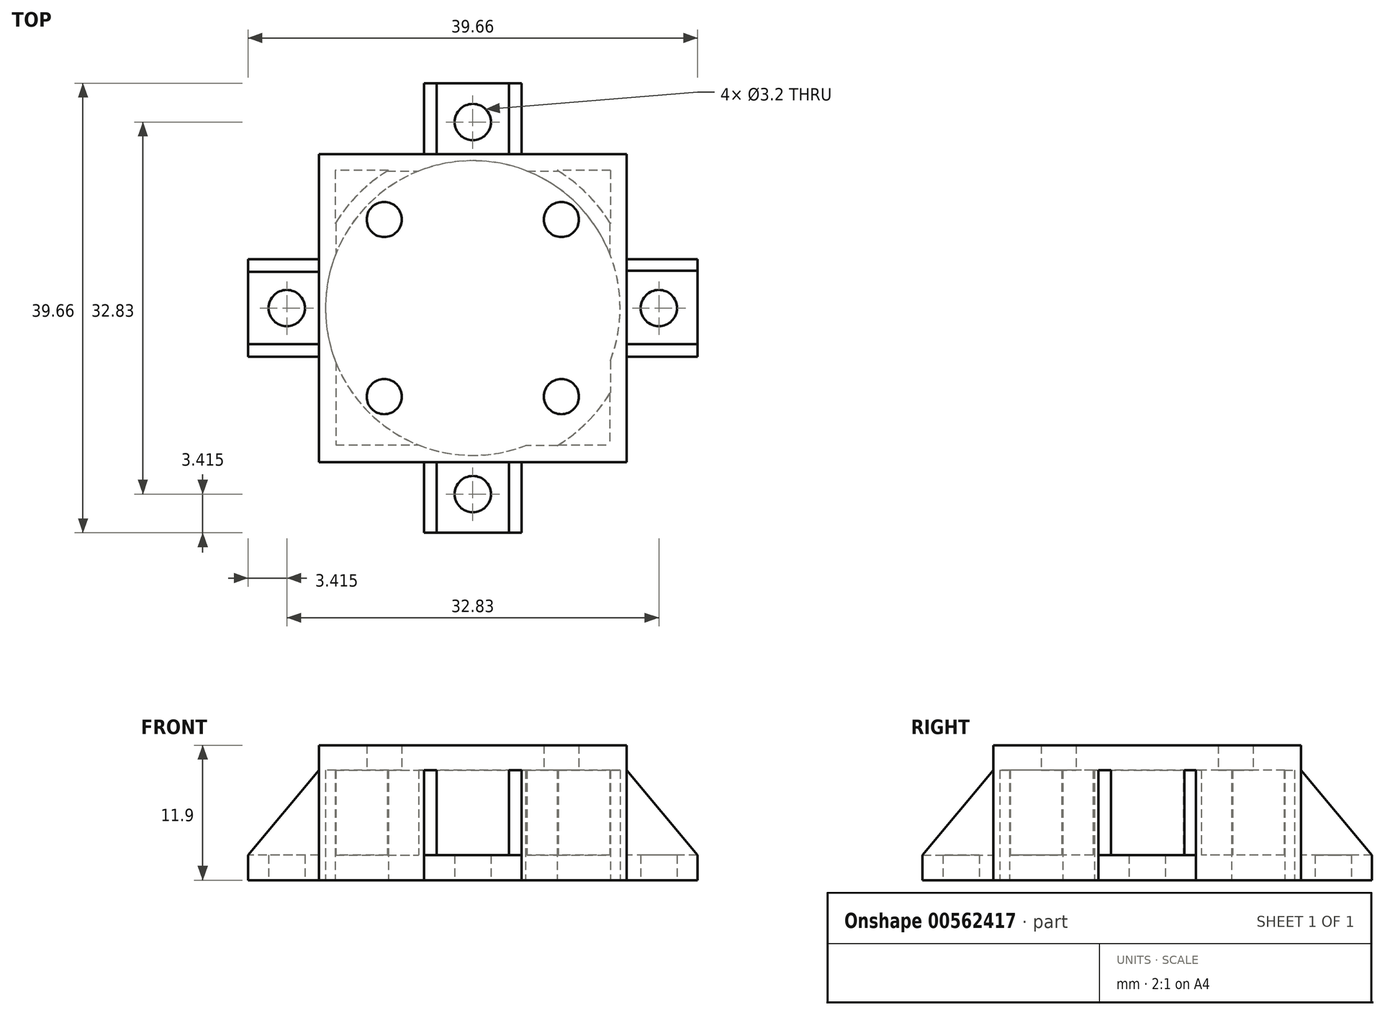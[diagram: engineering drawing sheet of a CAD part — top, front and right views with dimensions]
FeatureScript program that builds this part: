
annotation { "Feature Type Name" : "Feature", "Feature Type Description" : "" }
export const myFeature = defineFeature(function(context is Context, id is Id, definition is map)
    precondition{}
    {
        {
            var Q0;
            Q0=qCreatedBy(makeId("Top.planeOp"),FACE);
            var sketch = newSketch(context, id + "F0", { "sketchPlane" : qUnion([Q0])});
            skCircle(sketch, "E0", {"center": v(0, 0) * mm, "radius": 13 * mm});
            skLineSegment(sketch, "E1", {"start": v(0, 19.83) * mm, "end": v(4.3, 19.83) * mm});
            skLineSegment(sketch, "E2", {"start": v(4.3, 19.83) * mm, "end": v(4.3, 12.27) * mm});
            skLineSegment(sketch, "E3.MirrorCS", {"start": v(0, 19.83) * mm, "end": v(-4.3, 19.83) * mm});
            skLineSegment(sketch, "E4.MirrorCS", {"start": v(-4.3, 19.83) * mm, "end": v(-4.3, 12.27) * mm});
            skLineSegment(sketch, "E5", {"start": v(0, 0) * mm, "end": v(27.32, 0) * mm, "construction": true});
            skLineSegment(sketch, "E6", {"start": v(0, 0) * mm, "end": v(27.32, 27.32) * mm, "construction": true});
            skLineSegment(sketch, "E7", {"start": v(0, 19.83) * mm, "end": v(0, 13) * mm, "construction": true});
            skCircle(sketch, "E8", {"center": v(0, 16.42) * mm, "radius": 1.6 * mm});
            skLineSegment(sketch, "E9.MirrorCS", {"start": v(19.83, 0) * mm, "end": v(19.83, 4.3) * mm});
            skLineSegment(sketch, "E10.MirrorCS", {"start": v(19.83, 0) * mm, "end": v(19.83, -4.3) * mm});
            skLineSegment(sketch, "E11.MirrorCS", {"start": v(19.83, -4.3) * mm, "end": v(12.27, -4.3) * mm});
            skCircle(sketch, "E12.MirrorC", {"center": v(16.42, 0) * mm, "radius": 1.6 * mm});
            skLineSegment(sketch, "E13.MirrorCS", {"start": v(19.83, 4.3) * mm, "end": v(12.27, 4.3) * mm});
            skLineSegment(sketch, "E14.MirrorCS", {"start": v(0, -19.83) * mm, "end": v(4.3, -19.83) * mm});
            skLineSegment(sketch, "E15.MirrorCS", {"start": v(0, -19.83) * mm, "end": v(-4.3, -19.83) * mm});
            skLineSegment(sketch, "E16.MirrorCS", {"start": v(-4.3, -19.83) * mm, "end": v(-4.3, -12.27) * mm});
            skLineSegment(sketch, "E17.MirrorCS", {"start": v(4.3, -19.83) * mm, "end": v(4.3, -12.27) * mm});
            skCircle(sketch, "E18.MirrorC", {"center": v(0, -16.42) * mm, "radius": 1.6 * mm});
            skLineSegment(sketch, "E19", {"start": v(0, 0) * mm, "end": v(0, -28.1) * mm, "construction": true});
            skLineSegment(sketch, "E20.MirrorCS", {"start": v(-19.83, 4.3) * mm, "end": v(-12.27, 4.3) * mm});
            skLineSegment(sketch, "E21.MirrorCS", {"start": v(-19.83, 0) * mm, "end": v(-19.83, 4.3) * mm});
            skCircle(sketch, "E22.MirrorC", {"center": v(-16.42, 0) * mm, "radius": 1.6 * mm});
            skLineSegment(sketch, "E23.MirrorCS", {"start": v(-19.83, 0) * mm, "end": v(-19.83, -4.3) * mm});
            skLineSegment(sketch, "E24.MirrorCS", {"start": v(-19.83, -4.3) * mm, "end": v(-12.27, -4.3) * mm});
            skCircle(sketch, "E25", {"center": v(0, 0) * mm, "radius": 14.25 * mm});
            skLineSegment(sketch, "E26", {"start": v(-4.3, 13.59) * mm, "end": v(-13.59, 13.59) * mm});
            skLineSegment(sketch, "E27", {"start": v(-13.59, 13.59) * mm, "end": v(-13.59, 4.3) * mm});
            skLineSegment(sketch, "E28.MirrorCS", {"start": v(13.59, -4.3) * mm, "end": v(13.59, -13.59) * mm});
            skLineSegment(sketch, "E29.MirrorCS", {"start": v(13.59, -13.59) * mm, "end": v(4.3, -13.59) * mm});
            skLineSegment(sketch, "E30.MirrorCS", {"start": v(13.59, 4.3) * mm, "end": v(13.59, 13.59) * mm});
            skLineSegment(sketch, "E31.MirrorCS", {"start": v(13.59, 13.59) * mm, "end": v(4.3, 13.59) * mm});
            skLineSegment(sketch, "E32.MirrorCS", {"start": v(-4.3, -13.59) * mm, "end": v(-13.59, -13.59) * mm});
            skLineSegment(sketch, "E33.MirrorCS", {"start": v(-13.59, -13.59) * mm, "end": v(-13.59, -4.3) * mm});
            skLineSegment(sketch, "E34.bottom", {"start": v(12.14, 12.14) * mm, "end": v(-12.14, 12.14) * mm});
            skLineSegment(sketch, "E34.top", {"start": v(12.14, -12.14) * mm, "end": v(-12.14, -12.14) * mm});
            skLineSegment(sketch, "E34.left", {"start": v(12.14, 12.14) * mm, "end": v(12.14, -12.14) * mm});
            skLineSegment(sketch, "E34.right", {"start": v(-12.14, 12.14) * mm, "end": v(-12.14, -12.14) * mm});
            skSolve(sketch);
        }
        {
            var Q0;
            {var subQ5=sQuery(id+"F0.wireOp",EDGE,"E1");Q0=makeQuery(id+"F0.imprint","IMPRINT",FACE,{"disambiguationData":[TD([[makeQuery(id+"F0.imprint","IMPRINT",EDGE,{"derivedFrom":subQ5}),-1.0]])]});}
            var Q1;
            {var subQ0=sQuery(id+"F0.wireOp",EDGE,"E4.MirrorCS");var subQ1=sQuery(id+"F0.wireOp",EDGE,"E0");var subQ2=makeQuery(id+"F0.imprint","INTERSECT",VERTEX,{"derivedFrom":[subQ1,subQ0]});Q1=makeQuery(id+"F0.imprint","IMPRINT",FACE,{"disambiguationData":[TD([[makeQuery(id+"F0.imprint","IMPRINT",EDGE,{"disambiguationData":[TD([[subQ2,-1.0]])],"derivedFrom":subQ1}),-1.0]])]});}
            var Q2;
            {var subQ0=sQuery(id+"F0.wireOp",EDGE,"E2");var subQ1=sQuery(id+"F0.wireOp",EDGE,"E0");var subQ2=makeQuery(id+"F0.imprint","INTERSECT",VERTEX,{"derivedFrom":[subQ1,subQ0]});Q2=makeQuery(id+"F0.imprint","IMPRINT",FACE,{"disambiguationData":[TD([[makeQuery(id+"F0.imprint","IMPRINT",EDGE,{"disambiguationData":[TD([[subQ2,-1.0]])],"derivedFrom":subQ1}),-1.0]])]});}
            var Q3;
            {var subQ0=sQuery(id+"F0.wireOp",EDGE,"E2");var subQ1=sQuery(id+"F0.wireOp",EDGE,"E0");var subQ2=makeQuery(id+"F0.imprint","INTERSECT",VERTEX,{"derivedFrom":[subQ1,subQ0]});Q3=makeQuery(id+"F0.imprint","IMPRINT",FACE,{"disambiguationData":[TD([[makeQuery(id+"F0.imprint","IMPRINT",EDGE,{"disambiguationData":[TD([[subQ2,1.0]])],"derivedFrom":subQ1}),-1.0]])]});}
            var Q4;
            {var subQ0=sQuery(id+"F0.wireOp",EDGE,"E11.MirrorCS");var subQ1=sQuery(id+"F0.wireOp",EDGE,"E0");var subQ2=makeQuery(id+"F0.imprint","INTERSECT",VERTEX,{"derivedFrom":[subQ1,subQ0]});Q4=makeQuery(id+"F0.imprint","IMPRINT",FACE,{"disambiguationData":[TD([[makeQuery(id+"F0.imprint","IMPRINT",EDGE,{"disambiguationData":[TD([[subQ2,-1.0]])],"derivedFrom":subQ1}),-1.0]])]});}
            var Q5;
            {var subQ4=sQuery(id+"F0.wireOp",EDGE,"E9.MirrorCS");Q5=makeQuery(id+"F0.imprint","IMPRINT",FACE,{"disambiguationData":[TD([[makeQuery(id+"F0.imprint","IMPRINT",EDGE,{"derivedFrom":subQ4}),1.0]])]});}
            var Q6;
            {var subQ0=sQuery(id+"F0.wireOp",EDGE,"E11.MirrorCS");var subQ1=sQuery(id+"F0.wireOp",EDGE,"E0");var subQ2=makeQuery(id+"F0.imprint","INTERSECT",VERTEX,{"derivedFrom":[subQ1,subQ0]});Q6=makeQuery(id+"F0.imprint","IMPRINT",FACE,{"disambiguationData":[TD([[makeQuery(id+"F0.imprint","IMPRINT",EDGE,{"disambiguationData":[TD([[subQ2,1.0]])],"derivedFrom":subQ1}),-1.0]])]});}
            var Q7;
            {var subQ0=sQuery(id+"F0.wireOp",EDGE,"E16.MirrorCS");var subQ1=sQuery(id+"F0.wireOp",EDGE,"E0");var subQ2=makeQuery(id+"F0.imprint","INTERSECT",VERTEX,{"derivedFrom":[subQ1,subQ0]});Q7=makeQuery(id+"F0.imprint","IMPRINT",FACE,{"disambiguationData":[TD([[makeQuery(id+"F0.imprint","IMPRINT",EDGE,{"disambiguationData":[TD([[subQ2,-1.0]])],"derivedFrom":subQ1}),-1.0]])]});}
            var Q8;
            {var subQ0=sQuery(id+"F0.wireOp",EDGE,"E16.MirrorCS");var subQ1=sQuery(id+"F0.wireOp",EDGE,"E0");var subQ2=makeQuery(id+"F0.imprint","INTERSECT",VERTEX,{"derivedFrom":[subQ1,subQ0]});Q8=makeQuery(id+"F0.imprint","IMPRINT",FACE,{"disambiguationData":[TD([[makeQuery(id+"F0.imprint","IMPRINT",EDGE,{"disambiguationData":[TD([[subQ2,1.0]])],"derivedFrom":subQ1}),-1.0]])]});}
            var Q9;
            {var subQ0=sQuery(id+"F0.wireOp",EDGE,"E20.MirrorCS");var subQ1=sQuery(id+"F0.wireOp",EDGE,"E0");var subQ2=makeQuery(id+"F0.imprint","INTERSECT",VERTEX,{"derivedFrom":[subQ1,subQ0]});Q9=makeQuery(id+"F0.imprint","IMPRINT",FACE,{"disambiguationData":[TD([[makeQuery(id+"F0.imprint","IMPRINT",EDGE,{"disambiguationData":[TD([[subQ2,-1.0]])],"derivedFrom":subQ1}),-1.0]])]});}
            var Q10;
            {var subQ1=sQuery(id+"F0.wireOp",EDGE,"E21.MirrorCS");Q10=makeQuery(id+"F0.imprint","IMPRINT",FACE,{"disambiguationData":[TD([[makeQuery(id+"F0.imprint","IMPRINT",EDGE,{"derivedFrom":subQ1}),-1.0]])]});}
            var Q11;
            {var subQ1=sQuery(id+"F0.wireOp",EDGE,"E14.MirrorCS");Q11=makeQuery(id+"F0.imprint","IMPRINT",FACE,{"disambiguationData":[TD([[makeQuery(id+"F0.imprint","IMPRINT",EDGE,{"derivedFrom":subQ1}),1.0]])]});}
            var Q12;
            {var subQ0=sQuery(id+"F0.wireOp",EDGE,"E34.bottom");var subQ1=sQuery(id+"F0.wireOp",EDGE,"E25");var subQ2=makeQuery(id+"F0.imprint","INTERSECT",VERTEX,{"disambiguationData":[OD(1.0)],"derivedFrom":[subQ1,subQ0]});Q12=makeQuery(id+"F0.imprint","IMPRINT",FACE,{"disambiguationData":[TD([[makeQuery(id+"F0.imprint","IMPRINT",EDGE,{"disambiguationData":[TD([[subQ2,-1.0]])],"derivedFrom":subQ1}),-1.0]])]});}
            var Q13;
            {var subQ0=sQuery(id+"F0.wireOp",EDGE,"E32.MirrorCS");Q13=makeQuery(id+"F0.imprint","IMPRINT",FACE,{"disambiguationData":[TD([[makeQuery(id+"F0.imprint","IMPRINT",EDGE,{"derivedFrom":subQ0}),-1.0]])]});}
            var Q14;
            {var subQ0=sQuery(id+"F0.wireOp",EDGE,"E34.right");var subQ1=sQuery(id+"F0.wireOp",EDGE,"E25");var subQ2=makeQuery(id+"F0.imprint","INTERSECT",VERTEX,{"disambiguationData":[OD(1.0)],"derivedFrom":[subQ1,subQ0]});Q14=makeQuery(id+"F0.imprint","IMPRINT",FACE,{"disambiguationData":[TD([[makeQuery(id+"F0.imprint","IMPRINT",EDGE,{"disambiguationData":[TD([[subQ2,-1.0]])],"derivedFrom":subQ1}),-1.0]])]});}
            var Q15;
            {var subQ0=sQuery(id+"F0.wireOp",EDGE,"E24.MirrorCS");var subQ1=sQuery(id+"F0.wireOp",EDGE,"E0");var subQ2=makeQuery(id+"F0.imprint","INTERSECT",VERTEX,{"derivedFrom":[subQ1,subQ0]});Q15=makeQuery(id+"F0.imprint","IMPRINT",FACE,{"disambiguationData":[TD([[makeQuery(id+"F0.imprint","IMPRINT",EDGE,{"disambiguationData":[TD([[subQ2,-1.0]])],"derivedFrom":subQ1}),-1.0]])]});}
            var Q16;
            {var subQ7=sQuery(id+"F0.wireOp",EDGE,"E26");Q16=makeQuery(id+"F0.imprint","IMPRINT",FACE,{"disambiguationData":[TD([[makeQuery(id+"F0.imprint","IMPRINT",EDGE,{"derivedFrom":subQ7}),1.0]])]});}
            var Q17;
            {var subQ6=sQuery(id+"F0.wireOp",EDGE,"E30.MirrorCS");Q17=makeQuery(id+"F0.imprint","IMPRINT",FACE,{"disambiguationData":[TD([[makeQuery(id+"F0.imprint","IMPRINT",EDGE,{"derivedFrom":subQ6}),1.0]])]});}
            var Q18;
            {var subQ0=sQuery(id+"F0.wireOp",EDGE,"E34.left");var subQ1=sQuery(id+"F0.wireOp",EDGE,"E25");var subQ2=makeQuery(id+"F0.imprint","INTERSECT",VERTEX,{"disambiguationData":[OD(0.0)],"derivedFrom":[subQ1,subQ0]});Q18=makeQuery(id+"F0.imprint","IMPRINT",FACE,{"disambiguationData":[TD([[makeQuery(id+"F0.imprint","IMPRINT",EDGE,{"disambiguationData":[TD([[subQ2,-1.0]])],"derivedFrom":subQ1}),-1.0]])]});}
            var Q19;
            {var subQ0=sQuery(id+"F0.wireOp",EDGE,"E34.left");var subQ1=sQuery(id+"F0.wireOp",EDGE,"E0");var subQ2=makeQuery(id+"F0.imprint","INTERSECT",VERTEX,{"disambiguationData":[OD(0.0)],"derivedFrom":[subQ1,subQ0]});Q19=makeQuery(id+"F0.imprint","IMPRINT",FACE,{"disambiguationData":[TD([[makeQuery(id+"F0.imprint","IMPRINT",EDGE,{"disambiguationData":[TD([[subQ2,-1.0]])],"derivedFrom":subQ1}),-1.0]])]});}
            var Q20;
            {var subQ0=sQuery(id+"F0.wireOp",EDGE,"E13.MirrorCS");var subQ1=sQuery(id+"F0.wireOp",EDGE,"E0");var subQ2=makeQuery(id+"F0.imprint","INTERSECT",VERTEX,{"derivedFrom":[subQ1,subQ0]});Q20=makeQuery(id+"F0.imprint","IMPRINT",FACE,{"disambiguationData":[TD([[makeQuery(id+"F0.imprint","IMPRINT",EDGE,{"disambiguationData":[TD([[subQ2,-1.0]])],"derivedFrom":subQ1}),-1.0]])]});}
            var Q21;
            {var subQ0=sQuery(id+"F0.wireOp",EDGE,"E34.bottom");var subQ1=sQuery(id+"F0.wireOp",EDGE,"E0");var subQ2=makeQuery(id+"F0.imprint","INTERSECT",VERTEX,{"disambiguationData":[OD(1.0)],"derivedFrom":[subQ1,subQ0]});Q21=makeQuery(id+"F0.imprint","IMPRINT",FACE,{"disambiguationData":[TD([[makeQuery(id+"F0.imprint","IMPRINT",EDGE,{"disambiguationData":[TD([[subQ2,-1.0]])],"derivedFrom":subQ1}),-1.0]])]});}
            var Q22;
            {var subQ0=sQuery(id+"F0.wireOp",EDGE,"E20.MirrorCS");var subQ1=sQuery(id+"F0.wireOp",EDGE,"E0");var subQ2=makeQuery(id+"F0.imprint","INTERSECT",VERTEX,{"derivedFrom":[subQ1,subQ0]});Q22=makeQuery(id+"F0.imprint","IMPRINT",FACE,{"disambiguationData":[TD([[makeQuery(id+"F0.imprint","IMPRINT",EDGE,{"disambiguationData":[TD([[subQ2,1.0]])],"derivedFrom":subQ1}),-1.0]])]});}
            var Q23;
            {var subQ0=sQuery(id+"F0.wireOp",EDGE,"E34.right");var subQ1=sQuery(id+"F0.wireOp",EDGE,"E0");var subQ2=makeQuery(id+"F0.imprint","INTERSECT",VERTEX,{"disambiguationData":[OD(1.0)],"derivedFrom":[subQ1,subQ0]});Q23=makeQuery(id+"F0.imprint","IMPRINT",FACE,{"disambiguationData":[TD([[makeQuery(id+"F0.imprint","IMPRINT",EDGE,{"disambiguationData":[TD([[subQ2,-1.0]])],"derivedFrom":subQ1}),-1.0]])]});}
            var Q24;
            {var subQ0=sQuery(id+"F0.wireOp",EDGE,"E34.top");var subQ1=sQuery(id+"F0.wireOp",EDGE,"E0");var subQ2=makeQuery(id+"F0.imprint","INTERSECT",VERTEX,{"disambiguationData":[OD(1.0)],"derivedFrom":[subQ1,subQ0]});Q24=makeQuery(id+"F0.imprint","IMPRINT",FACE,{"disambiguationData":[TD([[makeQuery(id+"F0.imprint","IMPRINT",EDGE,{"disambiguationData":[TD([[subQ2,-1.0]])],"derivedFrom":subQ1}),-1.0]])]});}
            var Q25;
            {var subQ0=sQuery(id+"F0.wireOp",EDGE,"E34.top");var subQ1=sQuery(id+"F0.wireOp",EDGE,"E25");var subQ2=makeQuery(id+"F0.imprint","INTERSECT",VERTEX,{"disambiguationData":[OD(1.0)],"derivedFrom":[subQ1,subQ0]});Q25=makeQuery(id+"F0.imprint","IMPRINT",FACE,{"disambiguationData":[TD([[makeQuery(id+"F0.imprint","IMPRINT",EDGE,{"disambiguationData":[TD([[subQ2,-1.0]])],"derivedFrom":subQ1}),-1.0]])]});}
            var Q26;
            {var subQ0=sQuery(id+"F0.wireOp",EDGE,"E28.MirrorCS");Q26=makeQuery(id+"F0.imprint","IMPRINT",FACE,{"disambiguationData":[TD([[makeQuery(id+"F0.imprint","IMPRINT",EDGE,{"derivedFrom":subQ0}),-1.0]])]});}
            var Q27;
            {var subQ0=sQuery(id+"F0.wireOp",EDGE,"E17.MirrorCS");var subQ1=sQuery(id+"F0.wireOp",EDGE,"E0");var subQ2=makeQuery(id+"F0.imprint","INTERSECT",VERTEX,{"derivedFrom":[subQ1,subQ0]});Q27=makeQuery(id+"F0.imprint","IMPRINT",FACE,{"disambiguationData":[TD([[makeQuery(id+"F0.imprint","IMPRINT",EDGE,{"disambiguationData":[TD([[subQ2,-1.0]])],"derivedFrom":subQ1}),-1.0]])]});}
            extrude(context, id + "F1", {"entities" : qUnion([Q0, Q1, Q2, Q3, Q4, Q5, Q6, Q7, Q8, Q9, Q10, Q11, Q12, Q13, Q14, Q15, Q16, Q17, Q18, Q19, Q20, Q21, Q22, Q23, Q24, Q25, Q26, Q27]), "depth" : 2.2 * mm, "offsetDistance" : 25 * mm});
        }
        {
            var Q0;
            Q0=makeQuery(id+"F1.opExtrude","CAP_FACE",FACE,{"disambiguationData":[OSD([sQuery(id+"F0.wireOp",EDGE,"E0"),sQuery(id+"F0.wireOp",EDGE,"E1"),sQuery(id+"F0.wireOp",EDGE,"E2"),sQuery(id+"F0.wireOp",EDGE,"E3.MirrorCS"),sQuery(id+"F0.wireOp",EDGE,"E4.MirrorCS"),sQuery(id+"F0.wireOp",EDGE,"E8"),sQuery(id+"F0.wireOp",EDGE,"E9.MirrorCS"),sQuery(id+"F0.wireOp",EDGE,"E10.MirrorCS"),sQuery(id+"F0.wireOp",EDGE,"E11.MirrorCS"),sQuery(id+"F0.wireOp",EDGE,"E12.MirrorC"),sQuery(id+"F0.wireOp",EDGE,"E13.MirrorCS"),sQuery(id+"F0.wireOp",EDGE,"E14.MirrorCS"),sQuery(id+"F0.wireOp",EDGE,"E15.MirrorCS"),sQuery(id+"F0.wireOp",EDGE,"E16.MirrorCS"),sQuery(id+"F0.wireOp",EDGE,"E17.MirrorCS"),sQuery(id+"F0.wireOp",EDGE,"E18.MirrorC"),sQuery(id+"F0.wireOp",EDGE,"E20.MirrorCS"),sQuery(id+"F0.wireOp",EDGE,"E21.MirrorCS"),sQuery(id+"F0.wireOp",EDGE,"E22.MirrorC"),sQuery(id+"F0.wireOp",EDGE,"E23.MirrorCS"),sQuery(id+"F0.wireOp",EDGE,"E24.MirrorCS"),sQuery(id+"F0.wireOp",EDGE,"E25")])],"isStart":false});
            var sketch = newSketch(context, id + "F2", { "sketchPlane" : qUnion([Q0])});
            skPoint(sketch, "E35.first.point", {"position": v(-13.59, 4.3) * mm});
            skPoint(sketch, "E35.second.point", {"position": v(4.3, 13.59) * mm});
            skPoint(sketch, "E35.third.point", {"position": v(4.3, -13.59) * mm});
            skLineSegment(sketch, "E36", {"start": v(-4.3, 13.59) * mm, "end": v(-4.3, 19.83) * mm});
            skLineSegment(sketch, "E37", {"start": v(-4.3, 19.83) * mm, "end": v(4.3, 19.83) * mm});
            skLineSegment(sketch, "E38", {"start": v(4.3, 19.83) * mm, "end": v(4.3, 13.59) * mm});
            skLineSegment(sketch, "E39", {"start": v(13.59, 4.3) * mm, "end": v(19.83, 4.3) * mm});
            skLineSegment(sketch, "E40", {"start": v(19.83, 4.3) * mm, "end": v(19.83, -4.3) * mm});
            skLineSegment(sketch, "E41", {"start": v(19.83, -4.3) * mm, "end": v(13.59, -4.3) * mm});
            skLineSegment(sketch, "E42", {"start": v(4.3, -19.83) * mm, "end": v(-4.3, -19.83) * mm});
            skLineSegment(sketch, "E43", {"start": v(-4.3, -19.83) * mm, "end": v(-4.3, -13.59) * mm});
            skLineSegment(sketch, "E44", {"start": v(-13.59, -4.3) * mm, "end": v(-19.83, -4.3) * mm});
            skLineSegment(sketch, "E45", {"start": v(-19.83, -4.3) * mm, "end": v(-19.83, 4.3) * mm});
            skLineSegment(sketch, "E46", {"start": v(-19.83, 4.3) * mm, "end": v(-13.59, 4.3) * mm});
            skLineSegment(sketch, "E47.0", {"start": v(-3.2, 13.59) * mm, "end": v(-3.2, 19.83) * mm});
            skLineSegment(sketch, "E48.0", {"start": v(3.2, 19.83) * mm, "end": v(3.2, 13.59) * mm});
            skLineSegment(sketch, "E49.0", {"start": v(13.59, 3.3) * mm, "end": v(19.83, 3.3) * mm});
            skLineSegment(sketch, "E50.0", {"start": v(19.83, -3.2) * mm, "end": v(13.59, -3.2) * mm});
            skLineSegment(sketch, "E51.0", {"start": v(3.2, -19.83) * mm, "end": v(3.2, -13.59) * mm});
            skLineSegment(sketch, "E52.0", {"start": v(-3.2, -19.83) * mm, "end": v(-3.2, -13.59) * mm});
            skLineSegment(sketch, "E53.0", {"start": v(-19.83, 3.2) * mm, "end": v(-13.59, 3.2) * mm});
            skLineSegment(sketch, "E54.0", {"start": v(-13.59, -3.2) * mm, "end": v(-19.83, -3.2) * mm});
            skLineSegment(sketch, "E55.bottom", {"start": v(-13.59, 13.59) * mm, "end": v(13.59, 13.59) * mm});
            skLineSegment(sketch, "E55.top", {"start": v(-13.59, -13.59) * mm, "end": v(13.59, -13.59) * mm});
            skLineSegment(sketch, "E55.left", {"start": v(-13.59, 13.59) * mm, "end": v(-13.59, -13.59) * mm});
            skLineSegment(sketch, "E55.right", {"start": v(13.59, 13.59) * mm, "end": v(13.59, -13.59) * mm});
            skLineSegment(sketch, "E56.0", {"start": v(-12.09, 12.09) * mm, "end": v(12.09, 12.09) * mm});
            skLineSegment(sketch, "E56.1", {"start": v(-12.09, 12.09) * mm, "end": v(-12.09, -12.09) * mm});
            skLineSegment(sketch, "E56.2", {"start": v(-12.09, -12.09) * mm, "end": v(12.09, -12.09) * mm});
            skLineSegment(sketch, "E56.3", {"start": v(12.09, 12.09) * mm, "end": v(12.09, -12.09) * mm});
            skSolve(sketch);
        }
        {
            var Q0;
            {var subQ0=sQuery(id+"F2.wireOp",EDGE,"E38");Q0=makeQuery(id+"F2.imprint","IMPRINT",FACE,{"disambiguationData":[TD([[makeQuery(id+"F2.imprint","IMPRINT",EDGE,{"derivedFrom":subQ0}),-1.0]])]});}
            var Q1;
            Q1=makeQuery(id+"F2.imprint","IMPRINT",FACE,{"disambiguationData":[TD([[makeQuery(id+"F2.imprint","IMPRINT",EDGE,{"derivedFrom":makeQuery(id+"F1.opExtrude","CAP_EDGE",EDGE,{"disambiguationData":[OSD([sQuery(id+"F0.wireOp",EDGE,"E0")])],"isStart":false})}),-1.0]])]});
            var Q2;
            {var subQ0=sQuery(id+"F2.wireOp",EDGE,"E36");Q2=makeQuery(id+"F2.imprint","IMPRINT",FACE,{"disambiguationData":[TD([[makeQuery(id+"F2.imprint","IMPRINT",EDGE,{"derivedFrom":subQ0}),1.0]])]});}
            var Q3;
            {var subQ0=sQuery(id+"F2.wireOp",EDGE,"E39");Q3=makeQuery(id+"F2.imprint","IMPRINT",FACE,{"disambiguationData":[TD([[makeQuery(id+"F2.imprint","IMPRINT",EDGE,{"derivedFrom":subQ0}),1.0]])]});}
            var Q4;
            {var subQ0=sQuery(id+"F2.wireOp",EDGE,"E41");Q4=makeQuery(id+"F2.imprint","IMPRINT",FACE,{"disambiguationData":[TD([[makeQuery(id+"F2.imprint","IMPRINT",EDGE,{"derivedFrom":subQ0}),-1.0]])]});}
            var Q5;
            {var subQ0=sQuery(id+"F2.wireOp",EDGE,"E46");Q5=makeQuery(id+"F2.imprint","IMPRINT",FACE,{"disambiguationData":[TD([[makeQuery(id+"F2.imprint","IMPRINT",EDGE,{"derivedFrom":subQ0}),-1.0]])]});}
            var Q6;
            {var subQ0=sQuery(id+"F2.wireOp",EDGE,"E44");Q6=makeQuery(id+"F2.imprint","IMPRINT",FACE,{"disambiguationData":[TD([[makeQuery(id+"F2.imprint","IMPRINT",EDGE,{"derivedFrom":subQ0}),1.0]])]});}
            var Q7;
            {var subQ0=sQuery(id+"F2.wireOp",EDGE,"E43");Q7=makeQuery(id+"F2.imprint","IMPRINT",FACE,{"disambiguationData":[TD([[makeQuery(id+"F2.imprint","IMPRINT",EDGE,{"derivedFrom":subQ0}),-1.0]])]});}
            var Q8;
            {var subQ1=makeQuery(id+"F1.opExtrude","CAP_EDGE",EDGE,{"disambiguationData":[OSD([sQuery(id+"F0.wireOp",EDGE,"E17.MirrorCS")])],"isStart":false});Q8=makeQuery(id+"F2.imprint","IMPRINT",FACE,{"disambiguationData":[TD([[makeQuery(id+"F2.imprint","IMPRINT",EDGE,{"derivedFrom":subQ1}),1.0]])]});}
            extrude(context, id + "F3", {"entities" : qUnion([Q0, Q1, Q2, Q3, Q4, Q5, Q6, Q7, Q8]), "operationType" : NewBodyOperationType.ADD, "depth" : 7.5 * mm, "offsetDistance" : 25 * mm});
        }
        {
            var Q0;
            Q0=makeQuery(id+"F3.boolean.opBoolean","MERGE",FACE,{"derivedFrom":[makeQuery(id+"F1.opExtrude","SWEPT_FACE",FACE,{"disambiguationData":[OSD([sQuery(id+"F0.wireOp",EDGE,"E24.MirrorCS")])]}),makeQuery(id+"F3.opExtrude","SWEPT_FACE",FACE,{"disambiguationData":[OSD([sQuery(id+"F2.wireOp",EDGE,"E44")])]})]});
            var sketch = newSketch(context, id + "F4", { "sketchPlane" : qUnion([Q0])});
            skLineSegment(sketch, "E57", {"start": v(-19.83, 0) * mm, "end": v(-19.83, 2.2) * mm, "construction": true});
            skLineSegment(sketch, "E58", {"start": v(-19.83, 2.2) * mm, "end": v(-19.83, 9.7) * mm});
            skLineSegment(sketch, "E59", {"start": v(-19.83, 2.2) * mm, "end": v(-13.59, 2.2) * mm});
            skLineSegment(sketch, "E60", {"start": v(-19.83, 2.2) * mm, "end": v(-13.59, 9.7) * mm});
            skLineSegment(sketch, "E61", {"start": v(-13.59, 9.7) * mm, "end": v(-13.59, 2.2) * mm});
            skSolve(sketch);
        }
        {
            var Q0;
            Q0=makeQuery(id+"F4.imprint","IMPRINT",FACE,{"disambiguationData":[TD([[makeQuery(id+"F4.imprint","IMPRINT",EDGE,{"derivedFrom":sQuery(id+"F4.wireOp",EDGE,"E58")}),1.0]])]});
            extrude(context, id + "F5", {"entities" : qUnion([Q0]), "operationType" : NewBodyOperationType.REMOVE, "endBound" : BoundingType.THROUGH_ALL, "oppositeDirection" : true, "depth" : 25 * mm, "offsetDistance" : 25 * mm});
        }
        {
            var Q0;
            Q0=makeQuery(id+"F3.boolean.opBoolean","MERGE",FACE,{"derivedFrom":[makeQuery(id+"F1.opExtrude","SWEPT_FACE",FACE,{"disambiguationData":[OSD([sQuery(id+"F0.wireOp",EDGE,"E11.MirrorCS")])]}),makeQuery(id+"F3.opExtrude","SWEPT_FACE",FACE,{"disambiguationData":[OSD([sQuery(id+"F2.wireOp",EDGE,"E41")])]})]});
            var sketch = newSketch(context, id + "F6", { "sketchPlane" : qUnion([Q0])});
            skLineSegment(sketch, "E62", {"start": v(13.59, 0) * mm, "end": v(13.59, 2.2) * mm, "construction": true});
            skLineSegment(sketch, "E63", {"start": v(13.59, 2.2) * mm, "end": v(19.83, 2.2) * mm});
            skLineSegment(sketch, "E64", {"start": v(19.83, 2.2) * mm, "end": v(19.83, 9.7) * mm});
            skLineSegment(sketch, "E65", {"start": v(19.83, 2.2) * mm, "end": v(13.59, 9.7) * mm});
            skLineSegment(sketch, "E66", {"start": v(13.59, 9.7) * mm, "end": v(13.59, 2.2) * mm});
            skSolve(sketch);
        }
        {
            var Q0;
            {var subQ0=sQuery(id+"F6.wireOp",EDGE,"E64");Q0=makeQuery(id+"F6.imprint","IMPRINT",FACE,{"disambiguationData":[TD([[makeQuery(id+"F6.imprint","IMPRINT",EDGE,{"derivedFrom":subQ0}),-1.0]])]});}
            extrude(context, id + "F7", {"entities" : qUnion([Q0]), "operationType" : NewBodyOperationType.REMOVE, "endBound" : BoundingType.THROUGH_ALL, "oppositeDirection" : true, "depth" : 25 * mm, "offsetDistance" : 25 * mm});
        }
        {
            var Q0;
            Q0=makeQuery(id+"F3.boolean.opBoolean","MERGE",FACE,{"derivedFrom":[makeQuery(id+"F1.opExtrude","SWEPT_FACE",FACE,{"disambiguationData":[OSD([sQuery(id+"F0.wireOp",EDGE,"E16.MirrorCS")])]}),makeQuery(id+"F3.opExtrude","SWEPT_FACE",FACE,{"disambiguationData":[OSD([sQuery(id+"F2.wireOp",EDGE,"E43")])]})]});
            var sketch = newSketch(context, id + "F8", { "sketchPlane" : qUnion([Q0])});
            skLineSegment(sketch, "E67", {"start": v(13.59, 0) * mm, "end": v(13.59, 2.2) * mm, "construction": true});
            skLineSegment(sketch, "E68", {"start": v(13.59, 2.2) * mm, "end": v(19.83, 2.2) * mm});
            skLineSegment(sketch, "E69", {"start": v(13.59, 9.7) * mm, "end": v(19.83, 2.2) * mm});
            skLineSegment(sketch, "E70", {"start": v(13.59, 9.7) * mm, "end": v(13.59, 2.2) * mm});
            skSolve(sketch);
        }
        {
            var Q0;
            {var subQ0=sQuery(id+"F8.wireOp",EDGE,"E69");Q0=makeQuery(id+"F8.imprint","IMPRINT",FACE,{"disambiguationData":[TD([[makeQuery(id+"F8.imprint","IMPRINT",EDGE,{"derivedFrom":subQ0}),1.0]])]});}
            extrude(context, id + "F9", {"entities" : qUnion([Q0]), "operationType" : NewBodyOperationType.REMOVE, "endBound" : BoundingType.THROUGH_ALL, "oppositeDirection" : true, "depth" : 25 * mm, "offsetDistance" : 25 * mm});
        }
        {
            var Q0;
            Q0=makeQuery(id+"F3.boolean.opBoolean","MERGE",FACE,{"derivedFrom":[makeQuery(id+"F1.opExtrude","SWEPT_FACE",FACE,{"disambiguationData":[OSD([sQuery(id+"F0.wireOp",EDGE,"E4.MirrorCS")])]}),makeQuery(id+"F3.opExtrude","SWEPT_FACE",FACE,{"disambiguationData":[OSD([sQuery(id+"F2.wireOp",EDGE,"E36")])]})]});
            var sketch = newSketch(context, id + "F10", { "sketchPlane" : qUnion([Q0])});
            skLineSegment(sketch, "E71", {"start": v(-13.59, 0) * mm, "end": v(-13.59, 2.2) * mm, "construction": true});
            skLineSegment(sketch, "E72", {"start": v(-13.59, 2.2) * mm, "end": v(-19.83, 2.2) * mm});
            skLineSegment(sketch, "E73", {"start": v(-19.83, 2.2) * mm, "end": v(-19.83, 9.7) * mm});
            skLineSegment(sketch, "E74", {"start": v(-13.59, 2.2) * mm, "end": v(-13.59, 9.7) * mm});
            skLineSegment(sketch, "E75", {"start": v(-13.59, 9.7) * mm, "end": v(-19.83, 2.2) * mm});
            skSolve(sketch);
        }
        {
            var Q0;
            {var subQ0=sQuery(id+"F10.wireOp",EDGE,"E73");Q0=makeQuery(id+"F10.imprint","IMPRINT",FACE,{"disambiguationData":[TD([[makeQuery(id+"F10.imprint","IMPRINT",EDGE,{"derivedFrom":subQ0}),1.0]])]});}
            extrude(context, id + "F11", {"entities" : qUnion([Q0]), "operationType" : NewBodyOperationType.REMOVE, "endBound" : BoundingType.THROUGH_ALL, "oppositeDirection" : true, "depth" : 25 * mm, "offsetDistance" : 25 * mm});
        }
        {
            var Q0;
            Q0=makeQuery(id+"F3.opExtrude","CAP_FACE",FACE,{"disambiguationData":[OSD([sQuery(id+"F0.wireOp",EDGE,"E0"),sQuery(id+"F0.wireOp",EDGE,"E17.MirrorCS"),sQuery(id+"F2.wireOp",EDGE,"E35"),sQuery(id+"F2.wireOp",EDGE,"E36"),sQuery(id+"F2.wireOp",EDGE,"E37"),sQuery(id+"F2.wireOp",EDGE,"E38"),sQuery(id+"F2.wireOp",EDGE,"E39"),sQuery(id+"F2.wireOp",EDGE,"E40"),sQuery(id+"F2.wireOp",EDGE,"E41"),sQuery(id+"F2.wireOp",EDGE,"E42"),sQuery(id+"F2.wireOp",EDGE,"E43"),sQuery(id+"F2.wireOp",EDGE,"E44"),sQuery(id+"F2.wireOp",EDGE,"E45"),sQuery(id+"F2.wireOp",EDGE,"E46"),sQuery(id+"F2.wireOp",EDGE,"E47.0"),sQuery(id+"F2.wireOp",EDGE,"E48.0"),sQuery(id+"F2.wireOp",EDGE,"E49.0"),sQuery(id+"F2.wireOp",EDGE,"E50.0"),sQuery(id+"F2.wireOp",EDGE,"E51.0"),sQuery(id+"F2.wireOp",EDGE,"E52.0"),sQuery(id+"F2.wireOp",EDGE,"E53.0"),sQuery(id+"F2.wireOp",EDGE,"E54.0")])],"isStart":false});
            var sketch = newSketch(context, id + "F12", { "sketchPlane" : qUnion([Q0])});
            skPoint(sketch, "E76.first.point", {"position": v(-13.59, 4.3) * mm});
            skPoint(sketch, "E76.second.point", {"position": v(4.3, 13.59) * mm});
            skPoint(sketch, "E76.third.point", {"position": v(13.59, -4.3) * mm});
            skLineSegment(sketch, "E77", {"start": v(0, 0) * mm, "end": v(29.59, 0) * mm, "construction": true});
            skLineSegment(sketch, "E78", {"start": v(29.59, 29.59) * mm, "end": v(0, 0) * mm, "construction": true});
            skLineSegment(sketch, "E79", {"start": v(0, 0) * mm, "end": v(0, 30.25) * mm, "construction": true});
            skCircle(sketch, "E80", {"center": v(0, 0) * mm, "radius": 11.05 * mm, "construction": true});
            skCircle(sketch, "E81", {"center": v(7.81, 7.81) * mm, "radius": 1.55 * mm});
            skCircle(sketch, "E82.MirrorC", {"center": v(-7.81, 7.81) * mm, "radius": 1.55 * mm});
            skCircle(sketch, "E83.MirrorC", {"center": v(7.81, -7.81) * mm, "radius": 1.55 * mm});
            skCircle(sketch, "E84.MirrorC", {"center": v(-7.81, -7.81) * mm, "radius": 1.55 * mm});
            skLineSegment(sketch, "E85.bottom", {"start": v(-13.59, 13.59) * mm, "end": v(13.59, 13.59) * mm});
            skLineSegment(sketch, "E85.top", {"start": v(-13.59, -13.59) * mm, "end": v(13.59, -13.59) * mm});
            skLineSegment(sketch, "E85.left", {"start": v(-13.59, 13.59) * mm, "end": v(-13.59, -13.59) * mm});
            skLineSegment(sketch, "E85.right", {"start": v(13.59, 13.59) * mm, "end": v(13.59, -13.59) * mm});
            skSolve(sketch);
        }
        {
            var Q0;
            Q0=makeQuery(id+"F12.imprint","IMPRINT",FACE,{"disambiguationData":[TD([[makeQuery(id+"F12.imprint","IMPRINT",EDGE,{"derivedFrom":sQuery(id+"F12.wireOp",EDGE,"E81")}),-1.0]])]});
            var Q1;
            Q1=makeQuery(id+"F12.imprint","IMPRINT",FACE,{"disambiguationData":[TD([[makeQuery(id+"F12.imprint","IMPRINT",EDGE,{"derivedFrom":makeQuery(id+"F3.opExtrude","CAP_EDGE",EDGE,{"disambiguationData":[OSD([sQuery(id+"F0.wireOp",EDGE,"E0")])],"isStart":false})}),-1.0]])]});
            extrude(context, id + "F13", {"entities" : qUnion([Q0, Q1]), "operationType" : NewBodyOperationType.ADD, "depth" : 2.2 * mm, "offsetDistance" : 25 * mm});
        }
    });
